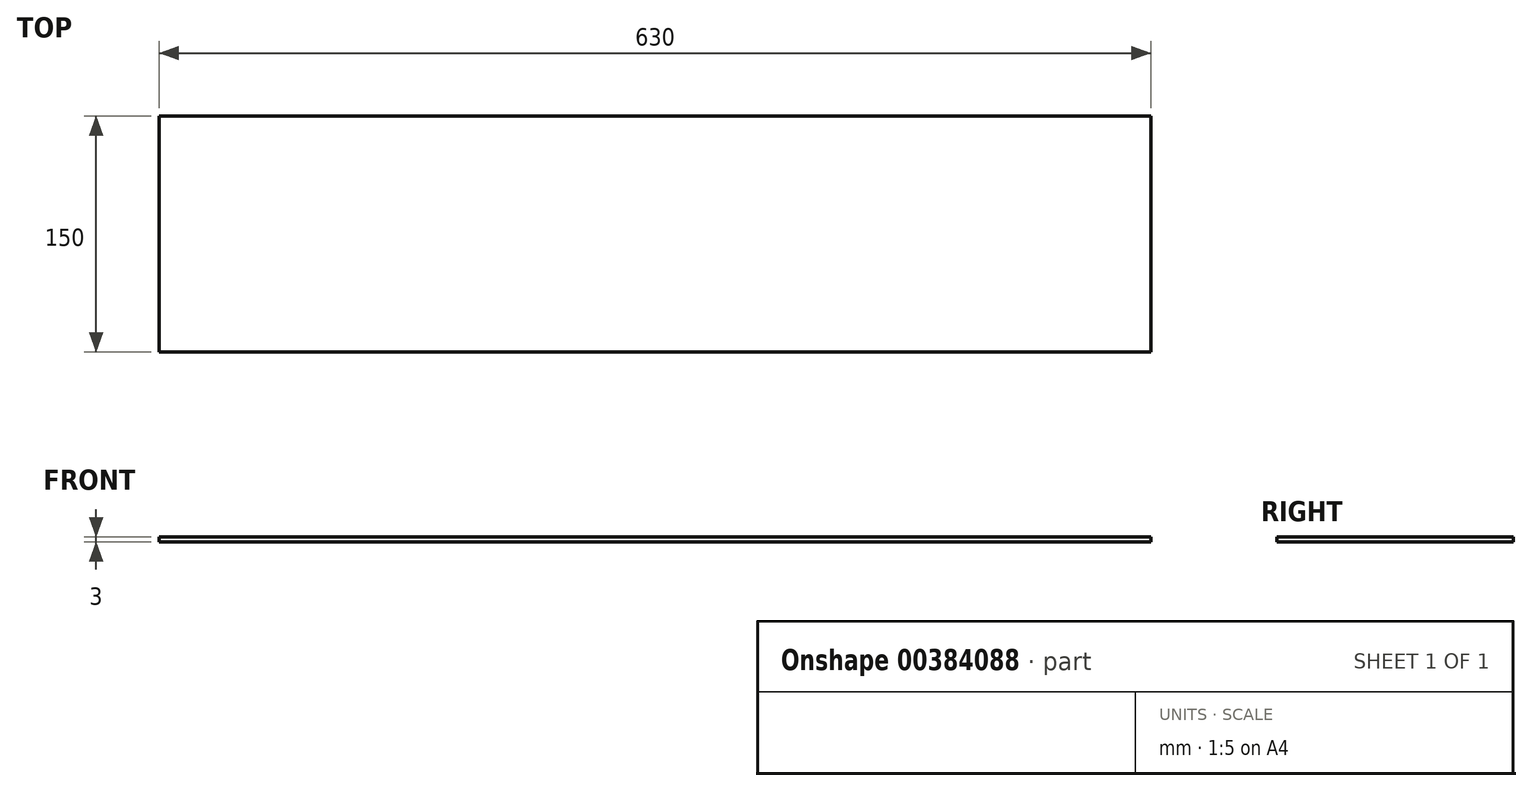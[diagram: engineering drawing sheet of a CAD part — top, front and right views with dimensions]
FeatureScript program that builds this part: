
annotation { "Feature Type Name" : "Feature", "Feature Type Description" : "" }
export const myFeature = defineFeature(function(context is Context, id is Id, definition is map)
    precondition{}
    {
        {
            var Q0;
            Q0=qCreatedBy(makeId("Top.planeOp"),FACE);
            var sketch = newSketch(context, id + "F0", { "sketchPlane" : qUnion([Q0])});
            skLineSegment(sketch, "E0.bottom", {"start": v(0, 0) * mm, "end": v(630, 0) * mm});
            skLineSegment(sketch, "E0.top", {"start": v(0, 150) * mm, "end": v(630, 150) * mm});
            skLineSegment(sketch, "E0.left", {"start": v(0, 0) * mm, "end": v(0, 150) * mm});
            skLineSegment(sketch, "E0.right", {"start": v(630, 0) * mm, "end": v(630, 150) * mm});
            skSolve(sketch);
        }
        {
            var Q0;
            Q0=makeQuery(id+"F0.imprint","IMPRINT",FACE,{"disambiguationData":[TD([[makeQuery(id+"F0.imprint","IMPRINT",EDGE,{"derivedFrom":sQuery(id+"F0.wireOp",EDGE,"E0.bottom")}),1.0]])]});
            extrude(context, id + "F1", {"entities" : qUnion([Q0]), "depth" : 3 * mm});
        }
    });
